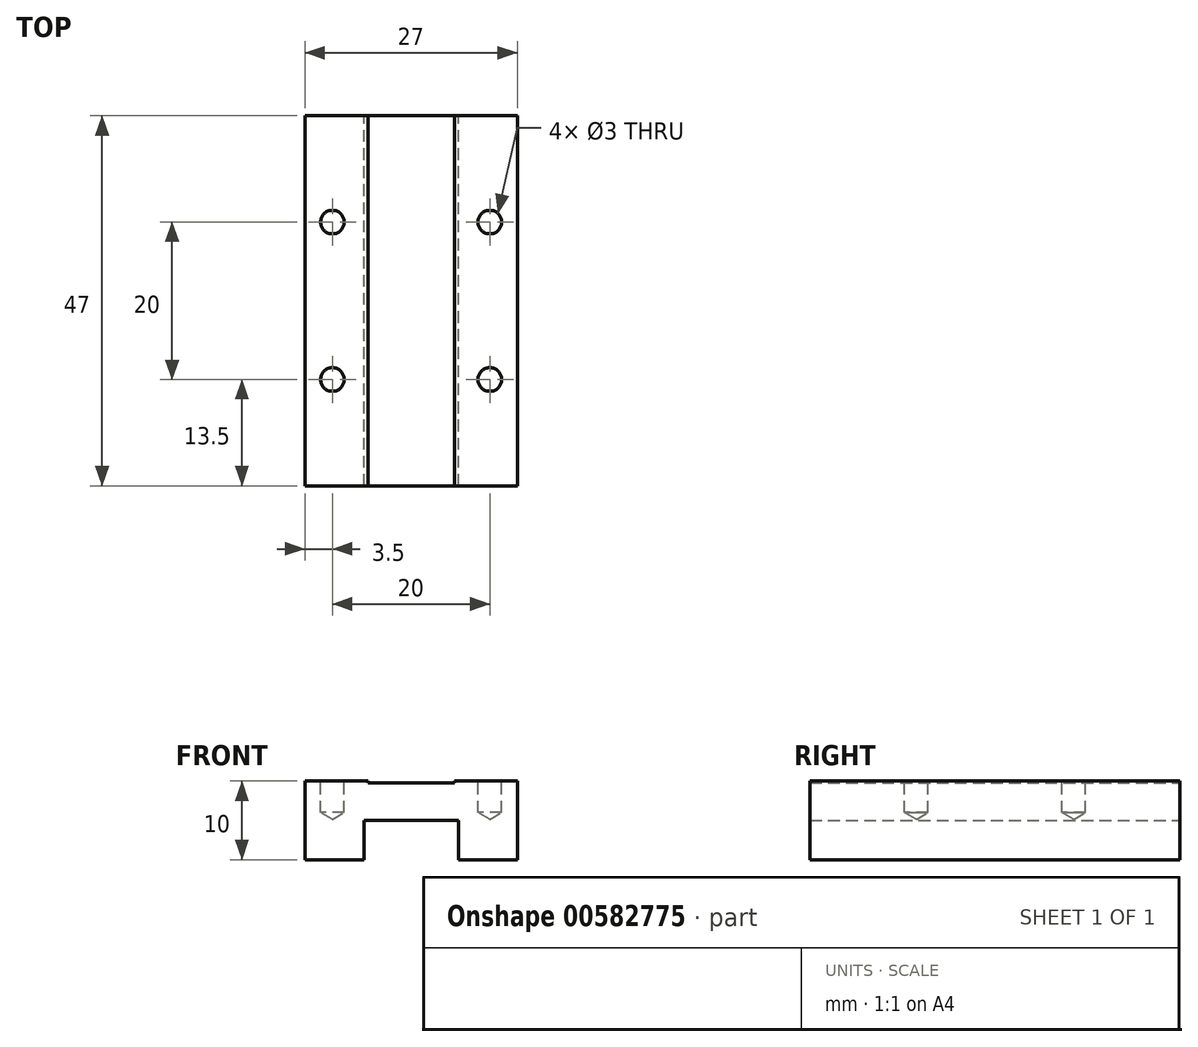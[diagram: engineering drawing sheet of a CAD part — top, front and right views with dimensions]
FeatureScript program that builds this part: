
annotation { "Feature Type Name" : "Feature", "Feature Type Description" : "" }
export const myFeature = defineFeature(function(context is Context, id is Id, definition is map)
    precondition{}
    {
        {
            var Q0;
            Q0=qCreatedBy(makeId("Front.planeOp"),FACE);
            var sketch = newSketch(context, id + "F0", { "sketchPlane" : qUnion([Q0])});
            skLineSegment(sketch, "E0.bottom", {"start": v(-13.5, 5) * mm, "end": v(-5.5, 5) * mm});
            skLineSegment(sketch, "E0.top", {"start": v(-13.5, -5) * mm, "end": v(-6, -5) * mm});
            skLineSegment(sketch, "E0.left", {"start": v(-13.5, 5) * mm, "end": v(-13.5, -5) * mm});
            skLineSegment(sketch, "E0.right", {"start": v(13.5, 5) * mm, "end": v(13.5, -5) * mm});
            skPoint(sketch, "E0.middle", {"position": v(0, 0) * mm});
            skLineSegment(sketch, "E1.bottom", {"start": v(-6, 0) * mm, "end": v(6, 0) * mm});
            skLineSegment(sketch, "E1.left", {"start": v(-6, 0) * mm, "end": v(-6, -5) * mm});
            skLineSegment(sketch, "E1.right", {"start": v(6, 0) * mm, "end": v(6, -5) * mm});
            skLineSegment(sketch, "E2.trimOffspring", {"start": v(6, -5) * mm, "end": v(13.5, -5) * mm});
            skLineSegment(sketch, "E3.top", {"start": v(-5.5, 4.75) * mm, "end": v(5.5, 4.75) * mm});
            skLineSegment(sketch, "E3.left", {"start": v(-5.5, 5) * mm, "end": v(-5.5, 4.75) * mm});
            skLineSegment(sketch, "E3.right", {"start": v(5.5, 5) * mm, "end": v(5.5, 4.75) * mm});
            skLineSegment(sketch, "E4.trimOffspring", {"start": v(5.5, 5) * mm, "end": v(13.5, 5) * mm});
            skSolve(sketch);
        }
        {
            var Q0;
            Q0=makeQuery(id+"F0.imprint","IMPRINT",FACE,{"disambiguationData":[TD([[makeQuery(id+"F0.imprint","IMPRINT",EDGE,{"derivedFrom":sQuery(id+"F0.wireOp",EDGE,"E0.bottom")}),-1.0]])]});
            extrude(context, id + "F1", {"entities" : qUnion([Q0]), "endBound" : BoundingType.SYMMETRIC, "depth" : 47 * mm, "offsetDistance" : 25 * mm});
        }
        {
            var Q0;
            Q0=makeQuery(id+"F1.opExtrude","SWEPT_FACE",FACE,{"disambiguationData":[OSD([sQuery(id+"F0.wireOp",EDGE,"E0.bottom")])]});
            var sketch = newSketch(context, id + "F2", { "sketchPlane" : qUnion([Q0])});
            skLineSegment(sketch, "E5.bottom", {"start": v(-10, 10) * mm, "end": v(10, 10) * mm, "construction": true});
            skLineSegment(sketch, "E5.top", {"start": v(-10, -10) * mm, "end": v(10, -10) * mm, "construction": true});
            skLineSegment(sketch, "E5.left", {"start": v(-10, 10) * mm, "end": v(-10, -10) * mm, "construction": true});
            skLineSegment(sketch, "E5.right", {"start": v(10, 10) * mm, "end": v(10, -10) * mm, "construction": true});
            skPoint(sketch, "E5.middle", {"position": v(0, 0) * mm});
            skSolve(sketch);
        }
        {
            var Q0;
            Q0=sQuery(id+"F2.wireOp",VERTEX,"E5.bottom.start");
            var Q1;
            Q1=sQuery(id+"F2.wireOp",VERTEX,"E5.bottom.end");
            var Q2;
            Q2=sQuery(id+"F2.wireOp",VERTEX,"E5.top.end");
            var Q3;
            Q3=sQuery(id+"F2.wireOp",VERTEX,"E5.top.start");
            var Q4;
            Q4=makeQuery(id+"F1.opExtrude","SWEPT_BODY",BODY,{"disambiguationData":[OSD([sQuery(id+"F0.wireOp",EDGE,"E0.bottom"),sQuery(id+"F0.wireOp",EDGE,"E0.top"),sQuery(id+"F0.wireOp",EDGE,"E0.left"),sQuery(id+"F0.wireOp",EDGE,"E0.right"),sQuery(id+"F0.wireOp",EDGE,"E1.bottom"),sQuery(id+"F0.wireOp",EDGE,"E1.left"),sQuery(id+"F0.wireOp",EDGE,"E1.right"),sQuery(id+"F0.wireOp",EDGE,"E2.trimOffspring"),sQuery(id+"F0.wireOp",EDGE,"E3.top"),sQuery(id+"F0.wireOp",EDGE,"E3.left"),sQuery(id+"F0.wireOp",EDGE,"E3.right"),sQuery(id+"F0.wireOp",EDGE,"E4.trimOffspring")])]});
            hole(context, id + "F3", {"style" : HoleStyle.SIMPLE, "endStyle" : HoleEndStyle.BLIND, "holeDiameter" : 3 * mm, "majorDiameter" : 5 * mm, "holeDepth" : 4 * mm, "isTappedThrough" : true, "tappedDepth" : 8 * mm, "tapClearance" : 3, "locations" : qUnion([Q0, Q1, Q2, Q3]), "scope" : qUnion([Q4])});
        }
    });
